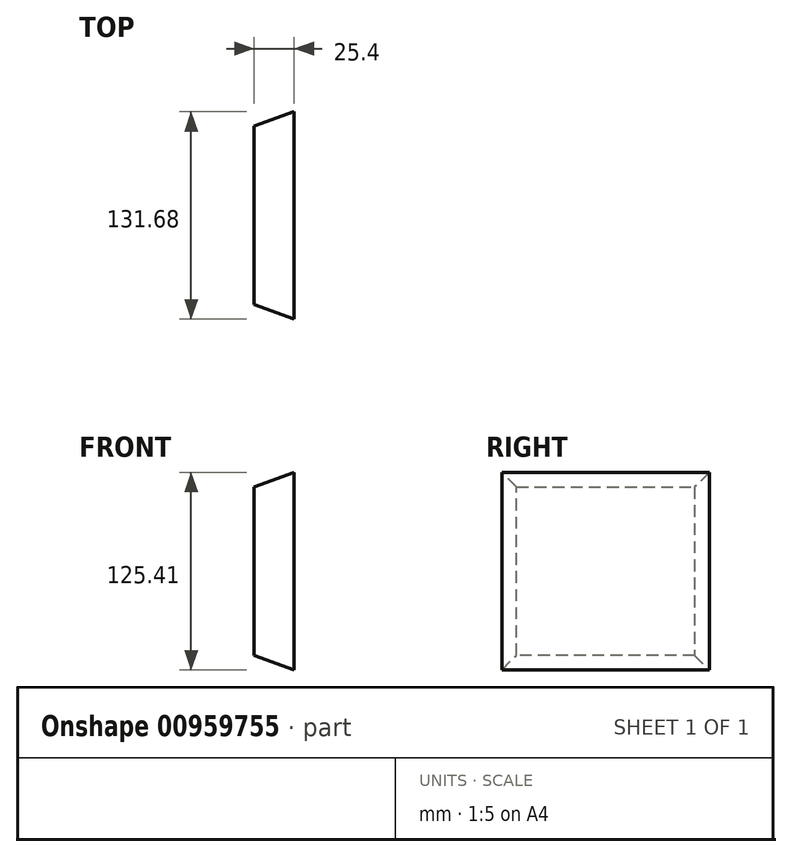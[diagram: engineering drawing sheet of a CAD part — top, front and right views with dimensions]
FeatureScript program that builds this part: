
annotation { "Feature Type Name" : "Feature", "Feature Type Description" : "" }
export const myFeature = defineFeature(function(context is Context, id is Id, definition is map)
    precondition{}
    {
        {
            var Q0;
            Q0=qCreatedBy(makeId("Right.planeOp"),FACE);
            var sketch = newSketch(context, id + "F0", { "sketchPlane" : qUnion([Q0])});
            skLineSegment(sketch, "E0.bottom", {"start": v(-43.89, 46.4) * mm, "end": v(69.3, 46.4) * mm});
            skLineSegment(sketch, "E0.top", {"start": v(-43.89, -60.52) * mm, "end": v(69.3, -60.52) * mm});
            skLineSegment(sketch, "E0.left", {"start": v(-43.89, 46.4) * mm, "end": v(-43.89, -60.52) * mm});
            skLineSegment(sketch, "E0.right", {"start": v(69.3, 46.4) * mm, "end": v(69.3, -60.52) * mm});
            skSolve(sketch);
        }
        {
            var Q0;
            Q0 = qSketchRegion(id + "F0", true);
            extrude(context, id + "F1", {"entities" : qUnion([Q0]), "depth" : 25.4 * mm, "offsetDistance" : 25.4 * mm, "hasDraft" : true, "draftAngle" : 20 * degree});
        }
    });
